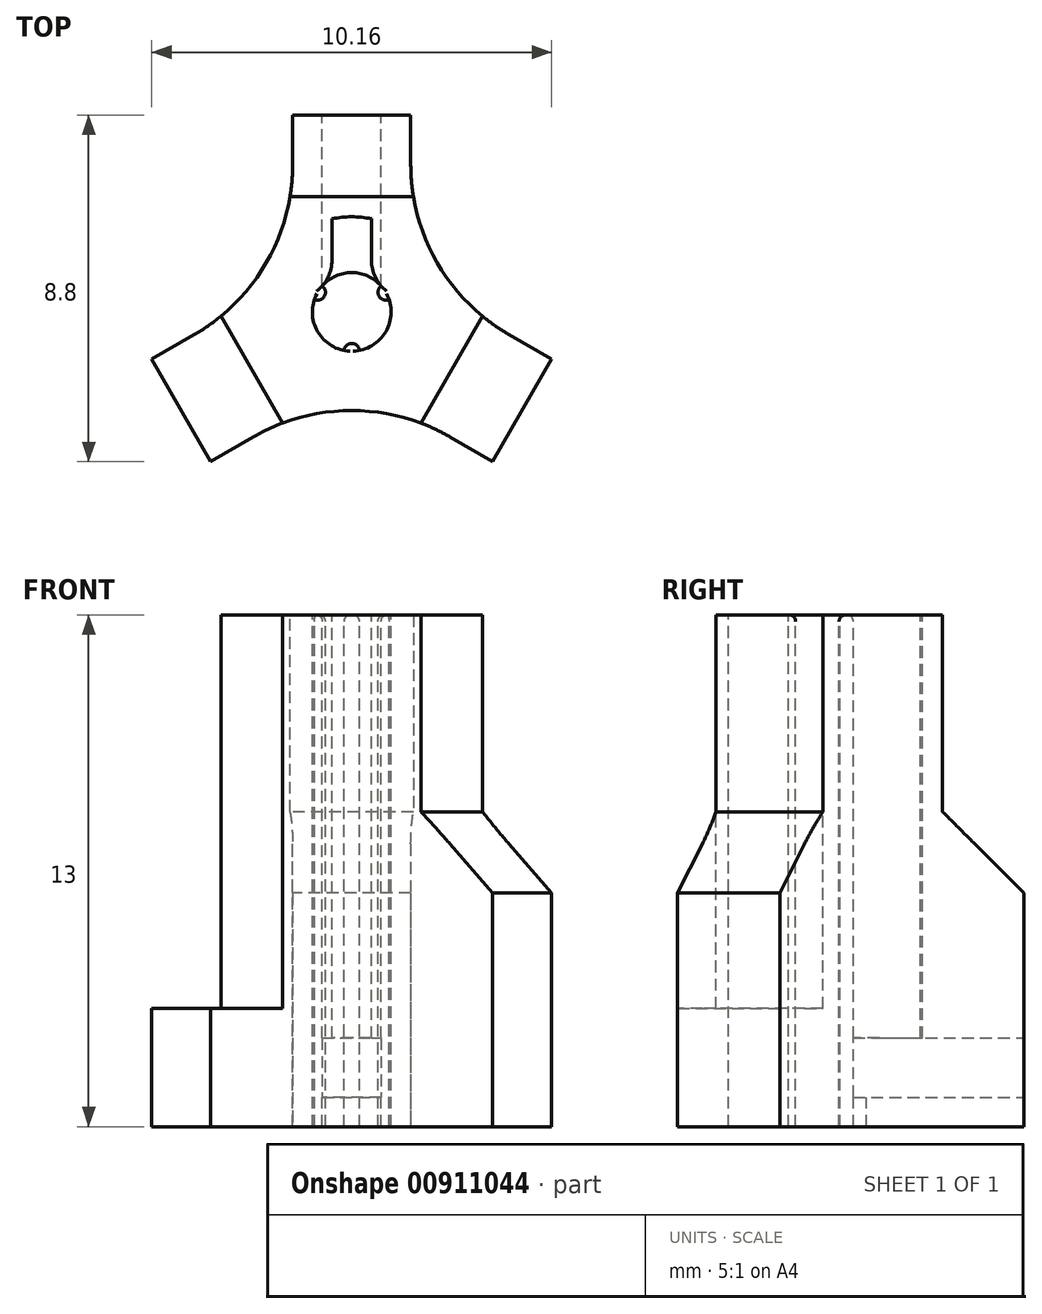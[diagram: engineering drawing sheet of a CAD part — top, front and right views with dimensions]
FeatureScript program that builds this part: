
annotation { "Feature Type Name" : "Feature", "Feature Type Description" : "" }
export const myFeature = defineFeature(function(context is Context, id is Id, definition is map)
    precondition{}
    {
        {
            var Q0;
            Q0=qCreatedBy(makeId("Top.planeOp"),FACE);
            var sketch = newSketch(context, id + "F0", { "sketchPlane" : qUnion([Q0])});
            skLineSegment(sketch, "E0.bottom", {"start": v(-1.5, 0) * mm, "end": v(1.5, 0) * mm});
            skLineSegment(sketch, "E0.top", {"start": v(-1.5, 5) * mm, "end": v(1.5, 5) * mm});
            skLineSegment(sketch, "E0.left", {"start": v(-1.5, 0) * mm, "end": v(-1.5, 5) * mm});
            skLineSegment(sketch, "E0.right", {"start": v(1.5, 0) * mm, "end": v(1.5, 5) * mm});
            skSolve(sketch);
        }
        {
            var Q0;
            Q0=makeQuery(id+"F0.imprint","IMPRINT",FACE,{"disambiguationData":[TD([[makeQuery(id+"F0.imprint","IMPRINT",EDGE,{"derivedFrom":sQuery(id+"F0.wireOp",EDGE,"E0.bottom")}),1.0]])]});
            extrude(context, id + "F1", {"entities" : qUnion([Q0]), "depth" : 3 * mm, "offsetDistance" : 25 * mm});
        }
        {
            var Q0;
            Q0=makeQuery(id+"F1.opExtrude","SWEPT_FACE",FACE,{"disambiguationData":[OSD([sQuery(id+"F0.wireOp",EDGE,"E0.bottom")])]});
            var sketch = newSketch(context, id + "F2", { "sketchPlane" : qUnion([Q0])});
            skLineSegment(sketch, "E1", {"start": v(0, 0) * mm, "end": v(0, 3) * mm});
            skSolve(sketch);
        }
        {
            var Q0;
            Q0=makeQuery(id+"F1.opExtrude","SWEPT_BODY",BODY,{"disambiguationData":[OSD([sQuery(id+"F0.wireOp",EDGE,"E0.bottom"),sQuery(id+"F0.wireOp",EDGE,"E0.top"),sQuery(id+"F0.wireOp",EDGE,"E0.left"),sQuery(id+"F0.wireOp",EDGE,"E0.right")])]});
            var Q1;
            Q1=sQuery(id+"F2.wireOp",EDGE,"E1");
            circularPattern(context, id + "F3", {"operationType" : NewBodyOperationType.ADD, "entities" : qUnion([Q0]), "axis" : qUnion([Q1]), "angle" : 360 * degree, "instanceCount" : 3, "equalSpace" : true});
        }
        {
            var Q0;
            {var subQ0=makeQuery(id+"F1.opExtrude","CAP_FACE",FACE,{"disambiguationData":[OSD([sQuery(id+"F0.wireOp",EDGE,"E0.bottom"),sQuery(id+"F0.wireOp",EDGE,"E0.top"),sQuery(id+"F0.wireOp",EDGE,"E0.left"),sQuery(id+"F0.wireOp",EDGE,"E0.right")])],"isStart":false});Q0=makeQuery(id+"F3.boolean.opBoolean","MERGE",FACE,{"derivedFrom":[subQ0,makeQuery(id+"F3.opPattern","COPY",FACE,{"derivedFrom":subQ0,"instanceName":"1"}),makeQuery(id+"F3.opPattern","COPY",FACE,{"derivedFrom":subQ0,"instanceName":"2"})]});}
            var sketch = newSketch(context, id + "F4", { "sketchPlane" : qUnion([Q0])});
            skArc(sketch, "E2", {"start": v(-0.95, 0.32) * mm, "mid": v(-0.87, -0.5) * mm, "end": v(-0.2, -0.98) * mm});
            skLineSegment(sketch, "E3", {"start": v(-1.5, 0.87) * mm, "end": v(0, 0) * mm, "construction": true});
            skLineSegment(sketch, "E4", {"start": v(0, 0) * mm, "end": v(1.5, 0.87) * mm, "construction": true});
            skLineSegment(sketch, "E5", {"start": v(0, -1.73) * mm, "end": v(0, 0) * mm, "construction": true});
            skArc(sketch, "E6.trimOffspring", {"start": v(0.75, 0.66) * mm, "mid": v(0, 1) * mm, "end": v(-0.75, 0.66) * mm});
            skArc(sketch, "E7.trimOffspring", {"start": v(0.2, -0.98) * mm, "mid": v(0.87, -0.5) * mm, "end": v(0.95, 0.32) * mm});
            skArc(sketch, "E8", {"start": v(-0.75, 0.66) * mm, "mid": v(-0.7, 0.4) * mm, "end": v(-0.95, 0.32) * mm});
            skArc(sketch, "E9", {"start": v(0.75, 0.66) * mm, "mid": v(0.7, 0.4) * mm, "end": v(0.95, 0.32) * mm});
            skArc(sketch, "E10", {"start": v(-0.2, -0.98) * mm, "mid": v(0, -0.8) * mm, "end": v(0.2, -0.98) * mm});
            skSolve(sketch);
        }
        {
            var Q0;
            Q0=makeQuery(id+"F4.imprint","IMPRINT",FACE,{"disambiguationData":[TD([[makeQuery(id+"F4.imprint","IMPRINT",EDGE,{"derivedFrom":sQuery(id+"F4.wireOp",EDGE,"E2")}),1.0]])]});
            var Q1;
            {var subQ0=makeQuery(id+"F1.opExtrude","CAP_FACE",FACE,{"disambiguationData":[OSD([sQuery(id+"F0.wireOp",EDGE,"E0.bottom"),sQuery(id+"F0.wireOp",EDGE,"E0.top"),sQuery(id+"F0.wireOp",EDGE,"E0.left"),sQuery(id+"F0.wireOp",EDGE,"E0.right")])],"isStart":true});Q1=makeQuery(id+"F3.boolean.opBoolean","MERGE",FACE,{"derivedFrom":[subQ0,makeQuery(id+"F3.opPattern","COPY",FACE,{"derivedFrom":subQ0,"instanceName":"1"}),makeQuery(id+"F3.opPattern","COPY",FACE,{"derivedFrom":subQ0,"instanceName":"2"})]});}
            extrude(context, id + "F5", {"entities" : qUnion([Q0]), "operationType" : NewBodyOperationType.REMOVE, "endBound" : BoundingType.UP_TO_SURFACE, "oppositeDirection" : true, "depth" : 25 * mm, "endBoundEntityFace" : qUnion([Q1]), "offsetDistance" : 25 * mm});
        }
        {
            var Q0;
            Q0=makeQuery(id+"F1.opExtrude","SWEPT_FACE",FACE,{"disambiguationData":[OSD([sQuery(id+"F0.wireOp",EDGE,"E0.top")])]});
            var sketch = newSketch(context, id + "F6", { "sketchPlane" : qUnion([Q0])});
            skLineSegment(sketch, "E11.0", {"start": v(-0.75, 2.25) * mm, "end": v(-0.75, 0.75) * mm});
            skLineSegment(sketch, "E11.1", {"start": v(0.75, 2.25) * mm, "end": v(-0.75, 2.25) * mm});
            skLineSegment(sketch, "E11.2", {"start": v(0.75, 2.25) * mm, "end": v(0.75, 0.75) * mm});
            skLineSegment(sketch, "E11.3", {"start": v(0.75, 0.75) * mm, "end": v(-0.75, 0.75) * mm});
            skSolve(sketch);
        }
        {
            var Q0;
            Q0 = qSketchRegion(id + "F6", true);
            var Q1;
            Q1=makeQuery(id+"F5.boolean.opBoolean","COPY",FACE,{"derivedFrom":makeQuery(id+"F5.opExtrude","SWEPT_FACE",FACE,{"disambiguationData":[OSD([sQuery(id+"F4.wireOp",EDGE,"E6.trimOffspring")])]})});
            extrude(context, id + "F7", {"entities" : qUnion([Q0]), "operationType" : NewBodyOperationType.REMOVE, "endBound" : BoundingType.UP_TO_SURFACE, "oppositeDirection" : true, "depth" : 25 * mm, "endBoundEntityFace" : qUnion([Q1]), "offsetDistance" : 25 * mm});
        }
        {
            var Q0;
            {var subQ0=makeQuery(id+"F1.opExtrude","CAP_FACE",FACE,{"disambiguationData":[OSD([sQuery(id+"F0.wireOp",EDGE,"E0.bottom"),sQuery(id+"F0.wireOp",EDGE,"E0.top"),sQuery(id+"F0.wireOp",EDGE,"E0.left"),sQuery(id+"F0.wireOp",EDGE,"E0.right")])],"isStart":false});Q0=makeQuery(id+"F3.boolean.opBoolean","MERGE",FACE,{"derivedFrom":[subQ0,makeQuery(id+"F3.opPattern","COPY",FACE,{"derivedFrom":subQ0,"instanceName":"1"}),makeQuery(id+"F3.opPattern","COPY",FACE,{"derivedFrom":subQ0,"instanceName":"2"})]});}
            var sketch = newSketch(context, id + "F8", { "sketchPlane" : qUnion([Q0])});
            skLineSegment(sketch, "E12.bottom", {"start": v(-0.5, 0.87) * mm, "end": v(0.5, 0.87) * mm});
            skLineSegment(sketch, "E12.top", {"start": v(-0.5, 2.37) * mm, "end": v(0.5, 2.37) * mm, "construction": true});
            skLineSegment(sketch, "E12.left", {"start": v(-0.5, 1.32) * mm, "end": v(-0.5, 2.37) * mm});
            skLineSegment(sketch, "E12.right", {"start": v(0.5, 1.32) * mm, "end": v(0.5, 2.37) * mm});
            skArc(sketch, "E13", {"start": v(-0.5, 2.37) * mm, "mid": v(0, 2.42) * mm, "end": v(0.5, 2.37) * mm});
            skArc(sketch, "E14", {"start": v(-0.75, 0.66) * mm, "mid": v(-0.56, 0.97) * mm, "end": v(-0.5, 1.32) * mm});
            skArc(sketch, "E15", {"start": v(0.5, 1.32) * mm, "mid": v(0.56, 0.97) * mm, "end": v(0.75, 0.66) * mm});
            skArc(sketch, "E16", {"start": v(0.5, 0.87) * mm, "mid": v(0.63, 0.77) * mm, "end": v(0.75, 0.66) * mm});
            skArc(sketch, "E17", {"start": v(-0.5, 0.87) * mm, "mid": v(-0.63, 0.77) * mm, "end": v(-0.75, 0.66) * mm});
            skSolve(sketch);
        }
        {
            var Q0;
            Q0=makeQuery(id+"F8.imprint","IMPRINT",FACE,{"disambiguationData":[TD([[makeQuery(id+"F8.imprint","IMPRINT",EDGE,{"derivedFrom":sQuery(id+"F8.wireOp",EDGE,"E12.left")}),-1.0]])]});
            var Q1;
            Q1=makeQuery(id+"F7.boolean.opBoolean","COPY",FACE,{"derivedFrom":makeQuery(id+"F7.opExtrude","SWEPT_FACE",FACE,{"disambiguationData":[OSD([sQuery(id+"F6.wireOp",EDGE,"E11.3")])]})});
            extrude(context, id + "F9", {"entities" : qUnion([Q0]), "operationType" : NewBodyOperationType.REMOVE, "endBound" : BoundingType.UP_TO_SURFACE, "oppositeDirection" : true, "depth" : 25 * mm, "endBoundEntityFace" : qUnion([Q1]), "offsetDistance" : 25 * mm});
        }
        {
            var Q0;
            {var subQ0=makeQuery(id+"F1.opExtrude","CAP_FACE",FACE,{"disambiguationData":[OSD([sQuery(id+"F0.wireOp",EDGE,"E0.bottom"),sQuery(id+"F0.wireOp",EDGE,"E0.top"),sQuery(id+"F0.wireOp",EDGE,"E0.left"),sQuery(id+"F0.wireOp",EDGE,"E0.right")])],"isStart":false});Q0=makeQuery(id+"F3.boolean.opBoolean","MERGE",FACE,{"derivedFrom":[subQ0,makeQuery(id+"F3.opPattern","COPY",FACE,{"derivedFrom":subQ0,"instanceName":"1"}),makeQuery(id+"F3.opPattern","COPY",FACE,{"derivedFrom":subQ0,"instanceName":"2"})]});}
            var sketch = newSketch(context, id + "F10", { "sketchPlane" : qUnion([Q0])});
            skLineSegment(sketch, "E18", {"start": v(-3.3, -0.17) * mm, "end": v(-1.8, -2.77) * mm});
            skLineSegment(sketch, "E19", {"start": v(1.8, -2.77) * mm, "end": v(3.3, -0.17) * mm});
            skLineSegment(sketch, "E20", {"start": v(-1.5, 2.93) * mm, "end": v(1.5, 2.93) * mm});
            skSolve(sketch);
        }
        {
            var Q0;
            {var subQ12=sQuery(id+"F10.wireOp",EDGE,"E18");Q0=makeQuery(id+"F10.imprint","IMPRINT",FACE,{"disambiguationData":[TD([[makeQuery(id+"F10.imprint","IMPRINT",EDGE,{"derivedFrom":subQ12}),1.0]])]});}
            extrude(context, id + "F11", {"entities" : qUnion([Q0]), "operationType" : NewBodyOperationType.ADD, "depth" : 10 * mm, "offsetDistance" : 25 * mm});
        }
        {
            var Q0;
            Q0=makeQuery(id+"F11.opExtrude","CAP_EDGE",EDGE,{"disambiguationData":[OSD([sQuery(id+"F10.wireOp",EDGE,"E18")])],"isStart":true});
            var Q1;
            Q1=makeQuery(id+"F11.opExtrude","CAP_EDGE",EDGE,{"disambiguationData":[OSD([sQuery(id+"F10.wireOp",EDGE,"E19")])],"isStart":true});
            var Q2;
            Q2=makeQuery(id+"F11.opExtrude","CAP_EDGE",EDGE,{"disambiguationData":[OSD([sQuery(id+"F10.wireOp",EDGE,"E20")])],"isStart":true});
            chamfer(context, id + "F12", {"entities" : qUnion([Q0, Q1, Q2]), "width" : 5 * mm, "tangentPropagation" : true});
        }
        {
            var Q0;
            {var subQ0=sQuery(id+"F0.wireOp",EDGE,"E0.left");var subQ1=sQuery(id+"F0.wireOp",EDGE,"E0.right");Q0=makeQuery(id+"F11.boolean.opBoolean","MERGE",EDGE,{"derivedFrom":[makeQuery(id+"F3.boolean.opBoolean","INTERSECT",EDGE,{"derivedFrom":[makeQuery(id+"F1.opExtrude","SWEPT_FACE",FACE,{"disambiguationData":[OSD([subQ1])]}),makeQuery(id+"F3.opPattern","COPY",FACE,{"derivedFrom":makeQuery(id+"F1.opExtrude","SWEPT_FACE",FACE,{"disambiguationData":[OSD([subQ0])]}),"instanceName":"2"})]}),makeQuery(id+"F11.opExtrude","SWEPT_EDGE",EDGE,{"disambiguationData":[OSD([subQ0,subQ1]),TDD([makeQuery(id+"F10.imprint","INTERSECT",VERTEX,{"derivedFrom":[makeQuery(id+"F1.opExtrude","CAP_EDGE",EDGE,{"disambiguationData":[OSD([subQ1])],"isStart":false}),makeQuery(id+"F3.opPattern","COPY",EDGE,{"derivedFrom":makeQuery(id+"F1.opExtrude","CAP_EDGE",EDGE,{"disambiguationData":[OSD([subQ0])],"isStart":false}),"instanceName":"2"})]})])]})]});}
            var Q1;
            {var subQ0=sQuery(id+"F0.wireOp",EDGE,"E0.right");var subQ1=sQuery(id+"F0.wireOp",EDGE,"E0.left");Q1=makeQuery(id+"F11.boolean.opBoolean","MERGE",EDGE,{"derivedFrom":[makeQuery(id+"F3.boolean.opBoolean","INTERSECT",EDGE,{"derivedFrom":[makeQuery(id+"F3.opPattern","COPY",FACE,{"derivedFrom":makeQuery(id+"F1.opExtrude","SWEPT_FACE",FACE,{"disambiguationData":[OSD([subQ1])]}),"instanceName":"1"}),makeQuery(id+"F3.opPattern","COPY",FACE,{"derivedFrom":makeQuery(id+"F1.opExtrude","SWEPT_FACE",FACE,{"disambiguationData":[OSD([subQ0])]}),"instanceName":"2"})]}),makeQuery(id+"F11.opExtrude","SWEPT_EDGE",EDGE,{"disambiguationData":[OSD([subQ1,subQ0]),TDD([makeQuery(id+"F10.imprint","INTERSECT",VERTEX,{"derivedFrom":[makeQuery(id+"F3.opPattern","COPY",EDGE,{"derivedFrom":makeQuery(id+"F1.opExtrude","CAP_EDGE",EDGE,{"disambiguationData":[OSD([subQ1])],"isStart":false}),"instanceName":"1"}),makeQuery(id+"F3.opPattern","COPY",EDGE,{"derivedFrom":makeQuery(id+"F1.opExtrude","CAP_EDGE",EDGE,{"disambiguationData":[OSD([subQ0])],"isStart":false}),"instanceName":"2"})]})])]})]});}
            var Q2;
            {var subQ0=sQuery(id+"F0.wireOp",EDGE,"E0.right");var subQ1=sQuery(id+"F0.wireOp",EDGE,"E0.left");Q2=makeQuery(id+"F11.boolean.opBoolean","MERGE",EDGE,{"derivedFrom":[makeQuery(id+"F3.boolean.opBoolean","INTERSECT",EDGE,{"derivedFrom":[makeQuery(id+"F1.opExtrude","SWEPT_FACE",FACE,{"disambiguationData":[OSD([subQ1])]}),makeQuery(id+"F3.opPattern","COPY",FACE,{"derivedFrom":makeQuery(id+"F1.opExtrude","SWEPT_FACE",FACE,{"disambiguationData":[OSD([subQ0])]}),"instanceName":"1"})]}),makeQuery(id+"F11.opExtrude","SWEPT_EDGE",EDGE,{"disambiguationData":[OSD([subQ1,subQ0]),TDD([makeQuery(id+"F10.imprint","INTERSECT",VERTEX,{"derivedFrom":[makeQuery(id+"F1.opExtrude","CAP_EDGE",EDGE,{"disambiguationData":[OSD([subQ1])],"isStart":false}),makeQuery(id+"F3.opPattern","COPY",EDGE,{"derivedFrom":makeQuery(id+"F1.opExtrude","CAP_EDGE",EDGE,{"disambiguationData":[OSD([subQ0])],"isStart":false}),"instanceName":"1"})]})])]})]});}
            fillet(context, id + "F13", {"entities" : qUnion([Q0, Q1, Q2]), "radius" : 5 * mm, "tangentPropagation" : true, "allowEdgeOverflow" : false});
        }
        {
            var Q0;
            Q0=makeQuery(id+"F11.opExtrude","CAP_EDGE",EDGE,{"disambiguationData":[OSD([sQuery(id+"F4.wireOp",EDGE,"E8")])],"isStart":false});
            var Q1;
            Q1=makeQuery(id+"F11.opExtrude","CAP_EDGE",EDGE,{"disambiguationData":[OSD([sQuery(id+"F4.wireOp",EDGE,"E9")])],"isStart":false});
            var Q2;
            Q2=makeQuery(id+"F11.opExtrude","CAP_EDGE",EDGE,{"disambiguationData":[OSD([sQuery(id+"F4.wireOp",EDGE,"E10")])],"isStart":false});
            fillet(context, id + "F14", {"entities" : qUnion([Q0, Q1, Q2]), "radius" : 0.16 * mm, "tangentPropagation" : true, "allowEdgeOverflow" : false});
        }
    });
